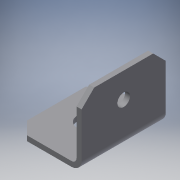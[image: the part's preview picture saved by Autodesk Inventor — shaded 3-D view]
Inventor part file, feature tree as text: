
AUTODESK INVENTOR PART (.ipt)
format: ipt  version: 2016 (Build 200138000, 138)  size: 136,704 bytes
history: native  units: mm
features: sheet_metal_op x4, other x4, sketch x4, hole x1, reference x1
ambient origin geometry x8: Origin, YZ Plane, XZ Plane, XY Plane, X Axis, Y Axis, Z Axis, Center Point
bodies: Solid1 (feature_tree)
feature tree (14):
  sheet_metal_op  "Face1"
  sheet_metal_op  "Flange1"
  other  "Corner Chamfer1"
  hole  "Hole1"  [1 undecoded]
  sketch  "Sketch1"  dims[d0=16.0mm d1=20.0mm]
  other  "Plate1"
  sketch  "Sketch2"  dims[d2=1.2mm]
  other  "Plate2"
  sheet_metal_op  "Bend1"
  sheet_metal_op  "Corner1"
  sketch  "Sketch3"  dims[d3=1.2mm]
  sketch  "Sketch4"  dims[d4=0.6mm d5=2.4mm d6=1.2mm d7=16.0mm d8=90.0deg d9=1.2mm d10=4.8mm d11=1.2mm d12=1.2mm d13=3.0mm d14=6.0mm d15=45.0deg d16=6.0mm d17=3.0mm d18=6.0mm d19=4.0mm d20=2.0mm d21=90.0deg d22=1.2mm d23=20.594885mm d24=0.4mm d25=1.2mm d26=0.0mm]
  reference  "Reference1"
  other  "Cut1"
note: 1 required parameter value undecoded (feature->parameter linkage not recoverable at this tier; creation-order binding heuristic only, values carry confidence <= 0.55)
